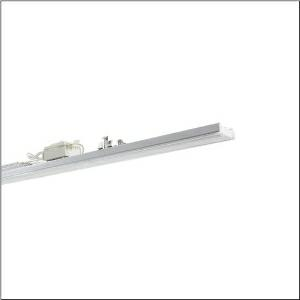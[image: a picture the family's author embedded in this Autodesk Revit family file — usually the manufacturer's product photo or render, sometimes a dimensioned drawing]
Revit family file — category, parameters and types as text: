
# Revit family: licross_r__11_recessed_ho_51te12dv4m2m3c_31f7
name_source: partatom
category: Lighting Fixtures
units: mm (PartAtom-declared; Revit-internal decimal feet)

## family parameters
Cut with Voids When Loaded = No
Host = Face
Light Source = No
Part Type = Normal
Room Calculation Point = No
Round Connector Dimension = Use Diameter
Shared = No

## types (1)
- --- (1 x LED, 1010 lm, 5.9 W, 4000K)
    Apparent Load = 6 VA
    CIE Flux Codes = 66 91 98 100 100
    Color Rendering = 80
    Color Temperature = 4000K
    Default Elevation = 1800 mm
    Description = Licross® 11 Recessed HO, luminaire insert, of sheet steel, galvanised, coil coated, white, length: 2.250mm, width: 66mm, height: 67mm, LED rated luminous flux: 27.150lm, light colour: 840, control gear: DALI 2 (for two DALI lines), with plug, 6-pole, with phase selection, for trunking rail, 14-core, mains connection: 220..240V, AC, 50/60Hz, rated input power: 154W, for trunking rail, 14-core, halogen-free wiring, for emergency light function, converter,control gear: single battery element, battery: LiFePO4, 9Ah, primary optical cover: cover, of PMMA, light emission: direct distribution, primary light characteristic: symmetric, protection rating (complete): IP54, insulation class (complete): insulation class I (protective earthing), certification: CE, UKCA, protection symbol: D if used in an environment with non-conductive dust loads with corresponding accessories, impact resistance: IK06, permissible ambient temperature for indoor applications: +5..+35°C, standard: EN 60598-2-22, LABS conformity tested according to VDMA 24364:2018-05, reducing of maximum allowable ambient temperature of 5°C with ceiling mounting, corresponds to IFS (International Featured Standards) requirements for safety and quality in the food industry, packaging unit: 1 piece
    Height = 58 mm
    Lamp = 1 x LED
    Lamp Light Flux = 1010 lm
    Lamp Power = 5.9 W
    Lamp count = 1
    Length = 2250 mm
    Luminous efficacy = 171 lm/W
    Manufacturer = Siteco
    ModVariant = No
    Model = 51TE12DV4M2M3C
    Mounting Place = Ceiling
    Mounting Type = Pendant
    Number of Poles = 1
    OnlyDefault = Yes
    Power Factor = 1
    Product Name = Licross® 11 Recessed HO
    Product group = luminaire insert
    ProductGroupID = 902
    Protection Class = Protection class I
    Protection Degree = IP 54
    RLX_Detail_Level = 1
    RLX_Emergency_Light_Flux = 0 lm
    RLX_Emergency_Type = 0
    RLX_Emergency_Type_DB = No
    RlxData = <blob elided: 30177 chars, md5=03715b5a>
    Socket = socket
    Standby Power = 0 W
    System Light Flux = 1010 lm
    System Power = 6 W
    Type Comments = : emergency light operation: 3 h
    Type Image = l_1296930.jpg
    URL = http://relux.com
    VarID = @adj_084766
    Voltage = 0 V
    Weight = 0.00 kg
    Width = 66 mm

## geometry (parser evidence)
native form markers: Blend x4, Sweep x10
no freeform markers — native parametric forms only
